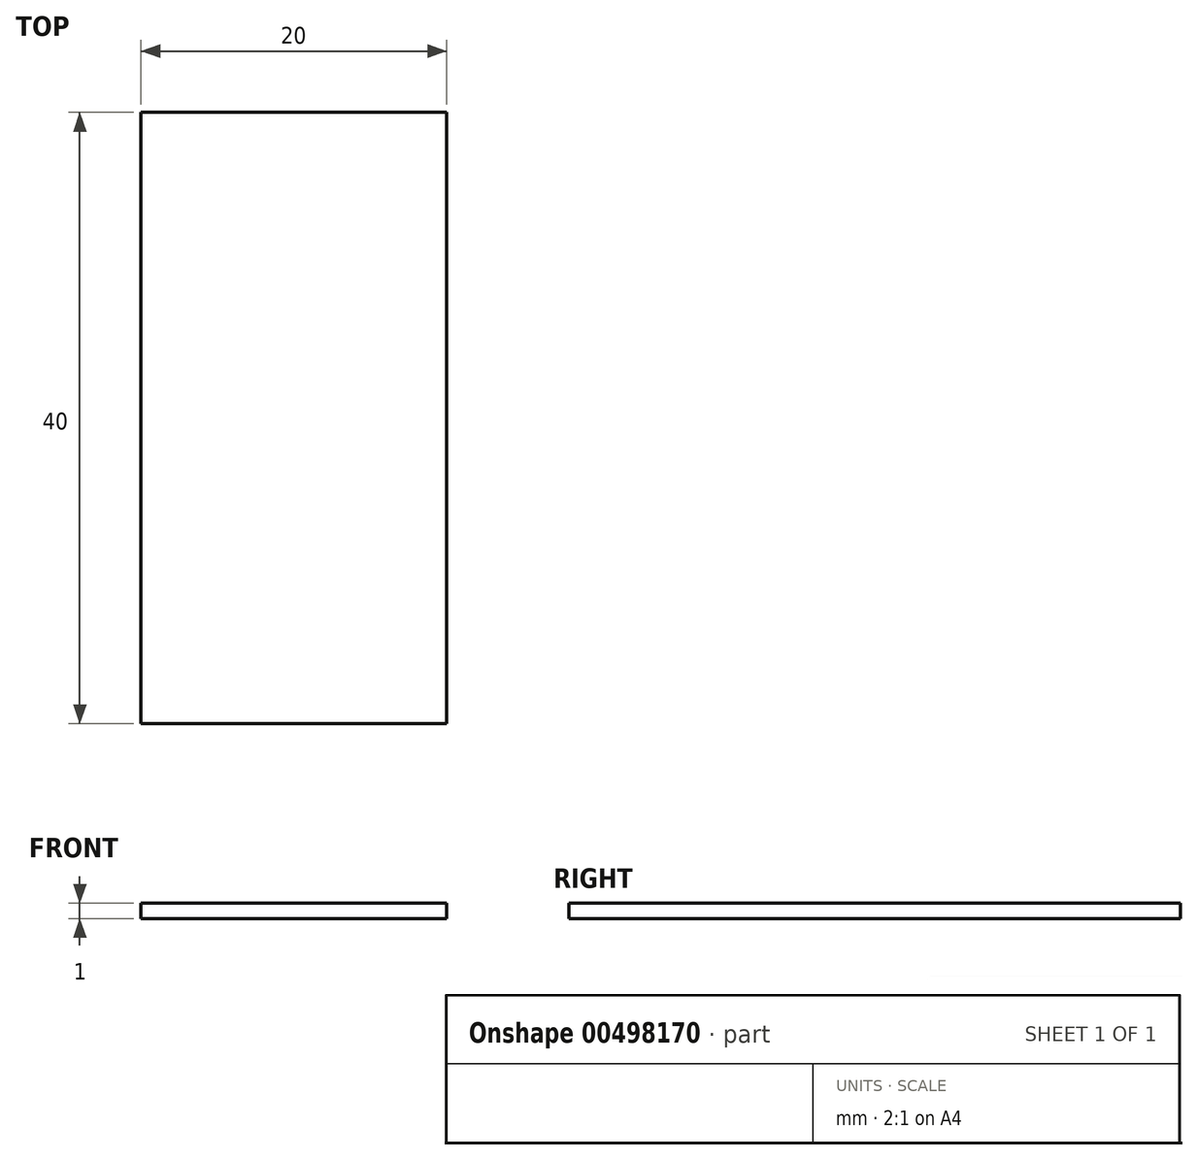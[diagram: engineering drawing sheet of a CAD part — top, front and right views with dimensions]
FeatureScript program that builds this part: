
annotation { "Feature Type Name" : "Feature", "Feature Type Description" : "" }
export const myFeature = defineFeature(function(context is Context, id is Id, definition is map)
    precondition{}
    {
        {
            var Q0;
            Q0=qCreatedBy(makeId("Top.planeOp"),FACE);
            var sketch = newSketch(context, id + "F0", { "sketchPlane" : qUnion([Q0])});
            skLineSegment(sketch, "E0.bottom", {"start": v(10, 20) * mm, "end": v(-10, 20) * mm});
            skLineSegment(sketch, "E0.top", {"start": v(10, -20) * mm, "end": v(-10, -20) * mm});
            skLineSegment(sketch, "E0.left", {"start": v(10, 20) * mm, "end": v(10, -20) * mm});
            skLineSegment(sketch, "E0.right", {"start": v(-10, 20) * mm, "end": v(-10, -20) * mm});
            skPoint(sketch, "E0.middle", {"position": v(0, 0) * mm});
            skSolve(sketch);
        }
        {
            var Q0;
            Q0 = qSketchRegion(id + "F0", true);
            extrude(context, id + "F1", {"entities" : qUnion([Q0]), "depth" : 1 * mm});
        }
    });
